# Revit family: Grohe_WallHungWC_BauCeramic_39351000
name_source: partatom
category: Plumbing Fixtures
units: mm (PartAtom-declared; Revit-internal decimal feet)

## family parameters
Cut with Voids When Loaded = No
Host = Face
OmniClass Number = 23.45.05.00
OmniClass Title = Sanitary Equipment
Part Type = Normal
Room Calculation Point = No
Round Connector Dimension = Use Diameter
Shared = No

## types (1)
- BAU CERAMIC Wall Hung WC (39351000)
    Assembly Code = D2041
    AssetType = Fixed
    BIMObjectName = Grohe_WallHungWC_BauCeramic_39351000
    CO2NeutralProduction = GROHE is one of the first leading manufacturer within the sanitary industry having a CO2-neutral production.
    ClassificationName = Uniclass2015
    ClassificationValue = Pr_40_20_93_94
    Color = White
    Cost = 0 $
    Default Elevation = 1219 mm
    Description = BAU CERAMIC Wall Hung WC
    DimensionsDocumentLink = https://cdn.cloud.grohe.com
    DocumentationCertificates = https://www.bimstore.co
    DocumentationInstallationGuide = https://www.bimstore.co
    DocumentationLiterature = https://www.bimstore.co
    DocumentationMaintenance = https://www.bimstore.co
    DocumentationTechnical = https://www.bimstore.co
    DurationUnit = Years
    EF000007 = White
    EF000008 = 304 mm
    EF000040 = 420 mm
    EF000049 = 531 mm
    EF001139 = Wall
    EF002169 = Ceramics
    EF002442 = Screw
    EF006009 = false
    EF006331 = false
    EF010237 = true
    EF010871 = 3
    EF011662 = Hard
    EF011663 = TRUE
    EF011664 = true
    EF011665 = false
    EF011668 = false
    EF011723 = true
    EF011724 = 180
    EF012545 = true
    EF020259 = PS (Pipe short)
    EF020295 = Deep
    EF020300 = Push button
    EF020712 = true
    EF020713 = false
    EF020714 = false
    EF020716 = false
    EF020717 = false
    EF020718 = true
    EF020719 = false
    EF021607 = false
    EF022280 = true
    EF022823 = Two quantities
    EF023789 = false
    EF023790 = false
    EF023829 = true
    EF024897 = Other
    Ecojoy = No
    ExpectedLife = 0
    FullRecyclabilityOfPlastic = All plastic components are fully recycable
    GROHESocialCommittment = green.grohe.com/social_engagement
    GROHESustainability = green.grohe.com
    IfcExportAs = IfcPipeFitting
    IfcExportType = IfcPipeFittingType
    Keynote = N44
    Manufacturer = Grohe
    ManufacturerName = Grohe
    Model = BAU CERAMIC Wall Hung WC
    ModelNumber = 39351000
    ModelReference = BAU CERAMIC Wall Hung WC
    NBSDescription = WC pans
    NBSObjectName = Grohe - WC pans
    NBSReference = 45-35-70/384
    NominalDepth = 0 mm  [stored 0 ft]
    NominalHeight = 0 mm  [stored 0 ft]
    NominalLength = 0 mm  [stored 0 ft]
    PrimaryMaterial = Grohe_White
    ProductDescription = consisting of:

Bau Ceramic wall hung WC (39 427 000)

for concealed cistern

horizontal outlet

wash down

rimless

flush volume 3/6 l

sanitary ware

Bau Ceramic WC seat (39 493 000)

soft close

quick release function

detachable

material: Duroplast

including fixation set
    ProductNumber = 39351000
    ProductShortText = BAU CERAMIC Wall Hung WC
    ProductType = WCs + Urinals
    ProductionYear = 2023
    SustainabilityAward = green.grohe.com/awards
    SustainabilityReport = green.grohe.com/reporting
    TPIDocumentLink = https://cdn.cloud.grohe.com
    Type Comments = BAU CERAMIC Wall Hung WC
    TypeName = BAU CERAMIC Wall Hung WC
    URL = https://www.grohe.co.uk
    WarrantyDurationLabor = 0
    WarrantyDurationParts = 0
    WarrantyDurationUnit = Years
    _BSBibleVersion = 17
    _BimSpecGuid = 0
    _CurrentRevision = 1
    _DistributedBy = https://www.bimstore.co
    _ObjectUserGuide = https://www.bimstore.co

note: [stored X ft] marks values corroborated as IEEE doubles in the binary element streams (Revit-internal decimal feet)

## geometry (parser evidence)
native form markers: Sweep x3
no freeform markers — native parametric forms only
